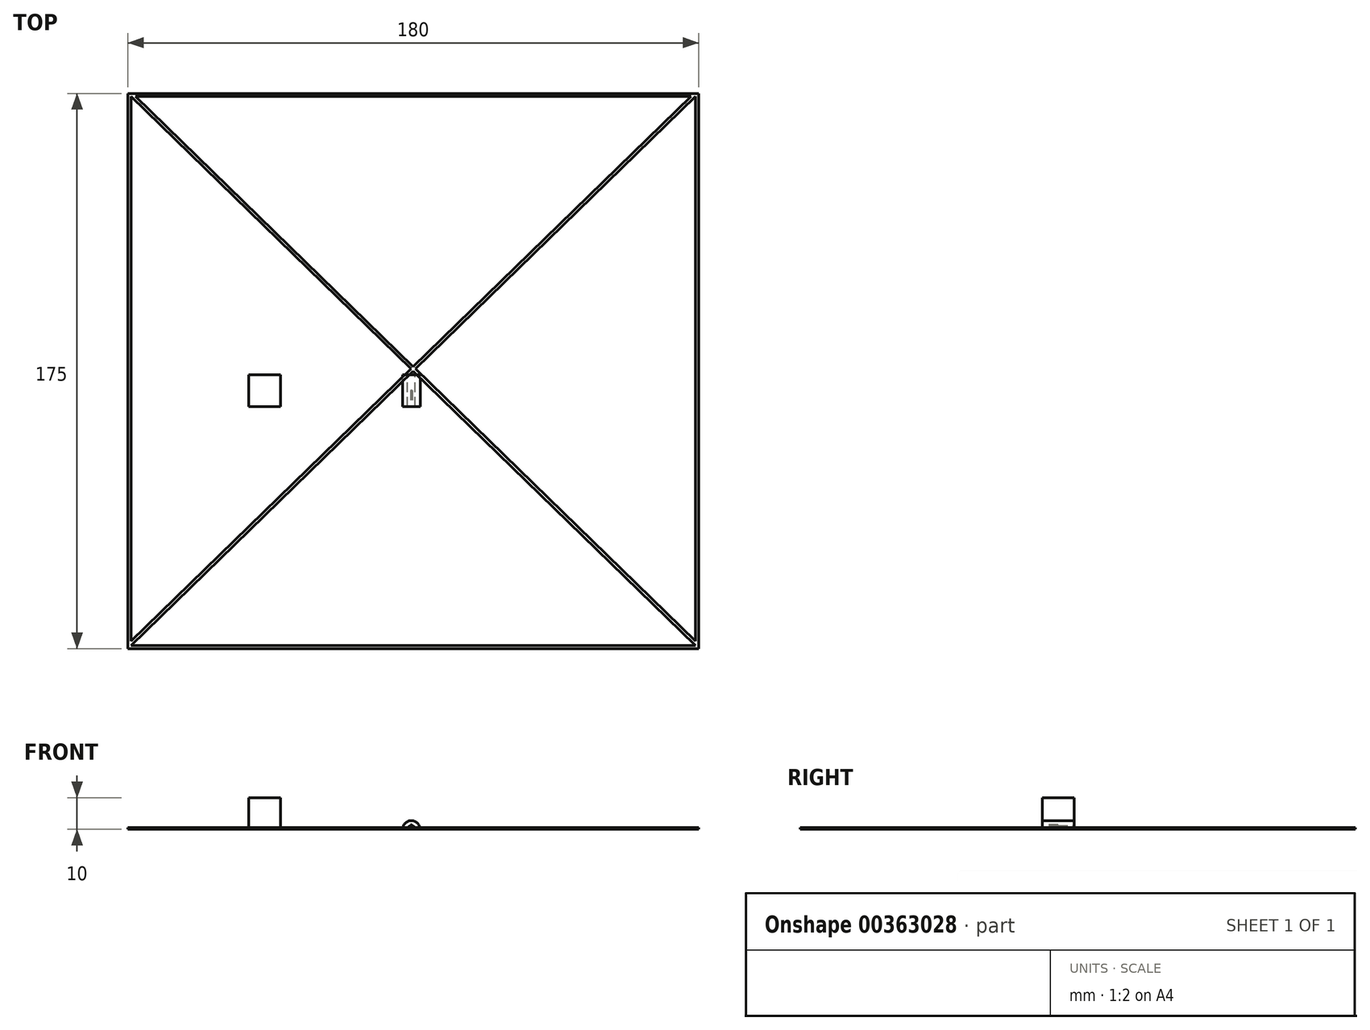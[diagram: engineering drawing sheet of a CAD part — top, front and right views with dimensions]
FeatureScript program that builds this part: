
annotation { "Feature Type Name" : "Feature", "Feature Type Description" : "" }
export const myFeature = defineFeature(function(context is Context, id is Id, definition is map)
    precondition{}
    {
        {
            var Q0;
            Q0=qCreatedBy(makeId("Front.planeOp"),FACE);
            var sketch = newSketch(context, id + "F0", { "sketchPlane" : qUnion([Q0])});
            skArc(sketch, "E0", {"start": v(2.75, 0) * mm, "mid": v(0, 2.75) * mm, "end": v(-2.75, 0) * mm});
            skArc(sketch, "E1", {"start": v(1.2, 0) * mm, "mid": v(0, 1.2) * mm, "end": v(-1.2, 0) * mm});
            skLineSegment(sketch, "E2", {"start": v(-2.75, 0) * mm, "end": v(-1.2, 0) * mm});
            skLineSegment(sketch, "E3.trimOffspring", {"start": v(1.2, 0) * mm, "end": v(2.75, 0) * mm});
            skSolve(sketch);
        }
        {
            var Q0;
            Q0 = qSketchRegion(id + "F0", true);
            extrude(context, id + "F1", {"entities" : qUnion([Q0]), "depth" : 5 * mm});
        }
        {
            var Q0;
            Q0=makeQuery(id+"F1.opExtrude","CAP_FACE",FACE,{"disambiguationData":[OSD([sQuery(id+"F0.wireOp",EDGE,"E0"),sQuery(id+"F0.wireOp",EDGE,"E1"),sQuery(id+"F0.wireOp",EDGE,"E2"),sQuery(id+"F0.wireOp",EDGE,"E3.trimOffspring")])],"isStart":false});
            var sketch = newSketch(context, id + "F2", { "sketchPlane" : qUnion([Q0])});
            skArc(sketch, "E4.0", {"start": v(1.2, 0) * mm, "mid": v(0, 1.2) * mm, "end": v(-1.2, 0) * mm});
            skArc(sketch, "E5.0", {"start": v(2.75, 0) * mm, "mid": v(0, 2.75) * mm, "end": v(-2.75, 0) * mm});
            skPoint(sketch, "E6.0", {"position": v(1.97, 0) * mm});
            skLineSegment(sketch, "E7.0", {"start": v(-2.75, 0) * mm, "end": v(-1.2, 0) * mm});
            skLineSegment(sketch, "E8.0", {"start": v(1.2, 0) * mm, "end": v(2.75, 0) * mm});
            skSolve(sketch);
        }
        {
            var Q0;
            Q0 = qSketchRegion(id + "F2", true);
            extrude(context, id + "F3", {"entities" : qUnion([Q0]), "operationType" : NewBodyOperationType.ADD, "depth" : 5 * mm});
        }
        {
            var Q0;
            Q0=makeQuery(id+"F3.opExtrude","CAP_FACE",FACE,{"disambiguationData":[OSD([sQuery(id+"F2.wireOp",EDGE,"E4.0"),sQuery(id+"F2.wireOp",EDGE,"E5.0"),sQuery(id+"F2.wireOp",EDGE,"E7.0"),sQuery(id+"F2.wireOp",EDGE,"E8.0")])],"isStart":false});
            var sketch = newSketch(context, id + "F4", { "sketchPlane" : qUnion([Q0])});
            skCircle(sketch, "E9", {"center": v(0, 1.2) * mm, "radius": 0.25 * mm});
            skSolve(sketch);
        }
        {
            var Q0;
            {var subQ0=sQuery(id+"F4.wireOp",EDGE,"E9");var subQ1=makeQuery(id+"F3.opExtrude","CAP_EDGE",EDGE,{"disambiguationData":[OSD([sQuery(id+"F2.wireOp",EDGE,"E4.0")])],"isStart":false});var subQ2=makeQuery(id+"F4.imprint","INTERSECT",VERTEX,{"disambiguationData":[OD(0.0)],"derivedFrom":[subQ1,subQ0]});Q0=makeQuery(id+"F4.imprint","IMPRINT",FACE,{"disambiguationData":[TD([[makeQuery(id+"F4.imprint","IMPRINT",EDGE,{"disambiguationData":[TD([[subQ2,-1.0]])],"derivedFrom":subQ0}),1.0]])]});}
            var Q1;
            Q1=sQuery(id+"F4.wireOp",EDGE,"E9");
            extrude(context, id + "F5", {"entities" : qUnion([Q0]), "operationType" : NewBodyOperationType.REMOVE, "surfaceEntities" : qUnion([Q1]), "oppositeDirection" : true, "depth" : 5 * mm});
        }
        {
            var Q0;
            Q0=qCreatedBy(makeId("Top.planeOp"), FACE);
            var sketch = newSketch(context, id + "F6", { "sketchPlane" : qUnion([Q0])});
            skLineSegment(sketch, "E10.bottom", {"start": v(-89.42, -86.3) * mm, "end": v(90.58, -86.3) * mm});
            skLineSegment(sketch, "E10.top", {"start": v(-89.42, 88.7) * mm, "end": v(90.58, 88.7) * mm});
            skLineSegment(sketch, "E10.left", {"start": v(-89.42, -86.3) * mm, "end": v(-89.42, 88.7) * mm});
            skLineSegment(sketch, "E10.right", {"start": v(90.58, -86.3) * mm, "end": v(90.58, 88.7) * mm});
            skLineSegment(sketch, "E11.0", {"start": v(-86.98, 87.7) * mm, "end": v(88.15, 87.7) * mm});
            skLineSegment(sketch, "E11.1", {"start": v(-88.42, -83.9) * mm, "end": v(-88.42, 87.7) * mm});
            skLineSegment(sketch, "E11.2", {"start": v(-88.42, -85.3) * mm, "end": v(89.58, -85.3) * mm});
            skLineSegment(sketch, "E11.3", {"start": v(89.58, -83.9) * mm, "end": v(89.58, 87.7) * mm});
            skLineSegment(sketch, "E12", {"start": v(-88.42, -85.3) * mm, "end": v(0.58, 1.2) * mm});
            skLineSegment(sketch, "E13", {"start": v(-88.42, 87.7) * mm, "end": v(-0.14, 1.9) * mm});
            skLineSegment(sketch, "E14.0", {"start": v(-86.98, 87.7) * mm, "end": v(0.58, 2.6) * mm});
            skLineSegment(sketch, "E15.0", {"start": v(-88.42, -83.9) * mm, "end": v(-0.14, 1.9) * mm});
            skLineSegment(sketch, "E16.trimOffspring", {"start": v(1.3, 1.9) * mm, "end": v(89.58, -83.9) * mm});
            skLineSegment(sketch, "E17.trimOffspring", {"start": v(0.58, 2.6) * mm, "end": v(88.15, 87.7) * mm});
            skLineSegment(sketch, "E18.trimOffspring", {"start": v(0.58, 1.2) * mm, "end": v(89.58, -85.3) * mm});
            skLineSegment(sketch, "E19.trimOffspring", {"start": v(1.3, 1.9) * mm, "end": v(89.58, 87.7) * mm});
            skSolve(sketch);
        }
        {
            var Q0;
            Q0 = qSketchRegion(id + "F6", true);
            extrude(context, id + "F7", {"entities" : qUnion([Q0]), "depth" : 0.5 * mm, "offsetDistance" : 25 * mm});
        }
        {
            var Q0;
            Q0=qCreatedBy(makeId("Top.planeOp"), FACE);
            var sketch = newSketch(context, id + "F8", { "sketchPlane" : qUnion([Q0])});
            skLineSegment(sketch, "E20.bottom", {"start": v(-51.23, 0) * mm, "end": v(-41.23, 0) * mm});
            skLineSegment(sketch, "E20.top", {"start": v(-51.23, -10) * mm, "end": v(-41.23, -10) * mm});
            skLineSegment(sketch, "E20.left", {"start": v(-51.23, 0) * mm, "end": v(-51.23, -10) * mm});
            skLineSegment(sketch, "E20.right", {"start": v(-41.23, 0) * mm, "end": v(-41.23, -10) * mm});
            skSolve(sketch);
        }
        {
            var Q0;
            Q0 = qSketchRegion(id + "F8", true);
            extrude(context, id + "F9", {"entities" : qUnion([Q0]), "depth" : 10 * mm, "offsetDistance" : 25 * mm});
        }
    });
